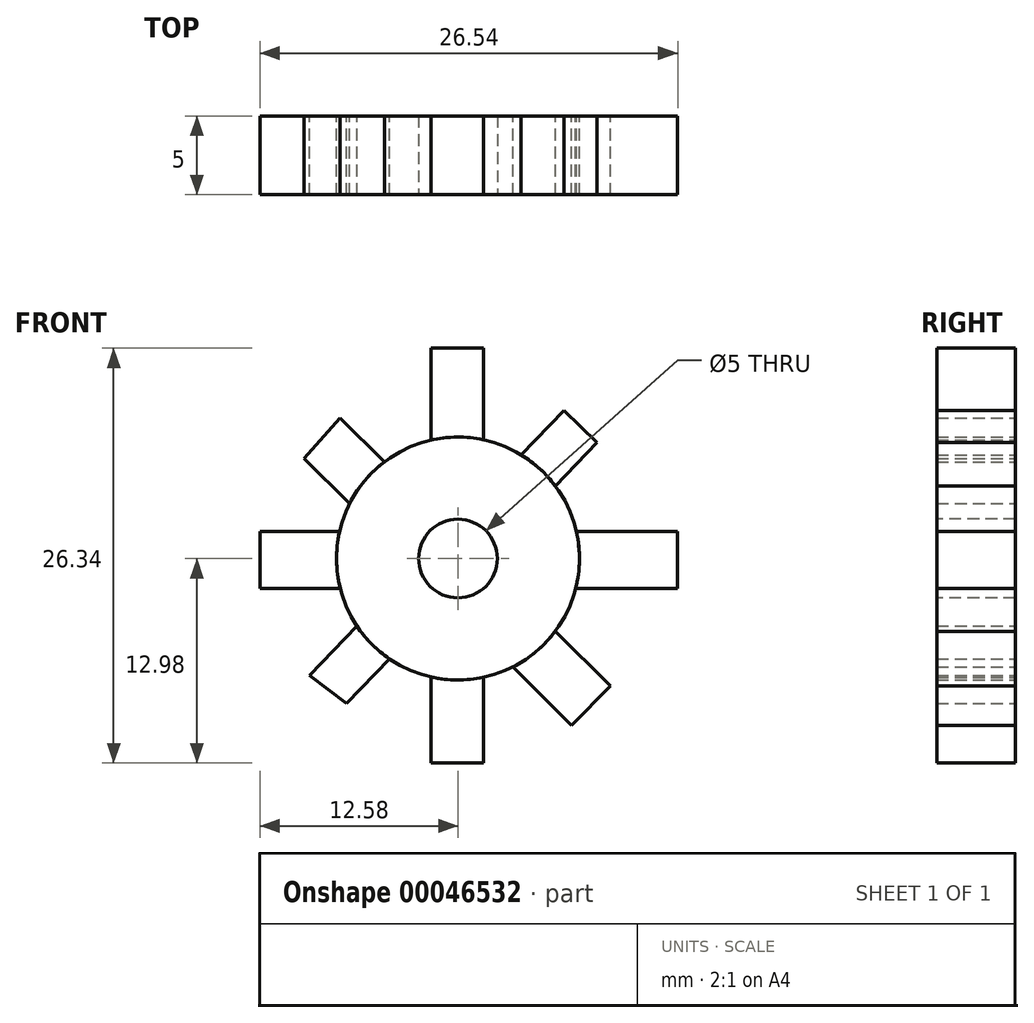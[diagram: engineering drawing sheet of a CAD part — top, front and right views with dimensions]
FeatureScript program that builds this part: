
annotation { "Feature Type Name" : "Feature", "Feature Type Description" : "" }
export const myFeature = defineFeature(function(context is Context, id is Id, definition is map)
    precondition{}
    {
        {
            var Q0;
            Q0=qCreatedBy(makeId("Front.planeOp"),FACE);
            var sketch = newSketch(context, id + "F0", { "sketchPlane" : qUnion([Q0])});
            skCircle(sketch, "E0", {"center": v(0, 0) * mm, "radius": 7.71 * mm});
            skSolve(sketch);
        }
        {
            var Q0;
            Q0=makeQuery(id+"F0.imprint","IMPRINT",FACE,{"disambiguationData":[TD([[makeQuery(id+"F0.imprint","IMPRINT",EDGE,{"derivedFrom":sQuery(id+"F0.wireOp",EDGE,"E0")}),1.0]])]});
            var sketch = newSketch(context, id + "F1", { "sketchPlane" : qUnion([Q0])});
            skLineSegment(sketch, "E1.bottom", {"start": v(-1.71, 13.36) * mm, "end": v(1.62, 13.36) * mm});
            skLineSegment(sketch, "E1.top", {"start": v(-1.71, -12.98) * mm, "end": v(1.62, -12.98) * mm});
            skLineSegment(sketch, "E1.left", {"start": v(-1.71, 13.36) * mm, "end": v(-1.71, -12.98) * mm});
            skLineSegment(sketch, "E1.right", {"start": v(1.62, 13.36) * mm, "end": v(1.62, -12.98) * mm});
            skSolve(sketch);
        }
        {
            var Q0;
            Q0=makeQuery(id+"F0.imprint","IMPRINT",FACE,{"disambiguationData":[TD([[makeQuery(id+"F0.imprint","IMPRINT",EDGE,{"derivedFrom":sQuery(id+"F0.wireOp",EDGE,"E0")}),1.0]])]});
            var sketch = newSketch(context, id + "F2", { "sketchPlane" : qUnion([Q0])});
            skLineSegment(sketch, "E2.bottom", {"start": v(-12.58, 1.7) * mm, "end": v(13.96, 1.7) * mm});
            skLineSegment(sketch, "E2.top", {"start": v(-12.58, -1.91) * mm, "end": v(13.96, -1.91) * mm});
            skLineSegment(sketch, "E2.left", {"start": v(-12.58, 1.7) * mm, "end": v(-12.58, -1.91) * mm});
            skLineSegment(sketch, "E2.right", {"start": v(13.96, 1.7) * mm, "end": v(13.96, -1.91) * mm});
            skSolve(sketch);
        }
        {
            var Q0;
            Q0=makeQuery(id+"F0.imprint","IMPRINT",FACE,{"disambiguationData":[TD([[makeQuery(id+"F0.imprint","IMPRINT",EDGE,{"derivedFrom":sQuery(id+"F0.wireOp",EDGE,"E0")}),1.0]])]});
            var sketch = newSketch(context, id + "F3", { "sketchPlane" : qUnion([Q0])});
            skLineSegment(sketch, "E3", {"start": v(-9.76, 6.37) * mm, "end": v(7.2, -10.6) * mm});
            skLineSegment(sketch, "E4", {"start": v(7.2, -10.6) * mm, "end": v(9.9, -7.9) * mm});
            skLineSegment(sketch, "E5", {"start": v(9.7, -8.1) * mm, "end": v(-7.48, 8.93) * mm});
            skLineSegment(sketch, "E6", {"start": v(-7.48, 8.93) * mm, "end": v(-9.76, 6.37) * mm});
            skSolve(sketch);
        }
        {
            var Q0;
            Q0=makeQuery(id+"F0.imprint","IMPRINT",FACE,{"disambiguationData":[TD([[makeQuery(id+"F0.imprint","IMPRINT",EDGE,{"derivedFrom":sQuery(id+"F0.wireOp",EDGE,"E0")}),1.0]])]});
            var sketch = newSketch(context, id + "F4", { "sketchPlane" : qUnion([Q0])});
            skLineSegment(sketch, "E7", {"start": v(-9.41, -7.41) * mm, "end": v(6.72, 9.41) * mm});
            skLineSegment(sketch, "E8", {"start": v(6.72, 9.41) * mm, "end": v(8.84, 7.38) * mm});
            skLineSegment(sketch, "E9", {"start": v(8.84, 7.38) * mm, "end": v(-7.07, -9.21) * mm});
            skLineSegment(sketch, "E10", {"start": v(-7.07, -9.21) * mm, "end": v(-9.41, -7.41) * mm});
            skSolve(sketch);
        }
        {
            var Q0;
            Q0=makeQuery(id+"F0.imprint","IMPRINT",FACE,{"disambiguationData":[TD([[makeQuery(id+"F0.imprint","IMPRINT",EDGE,{"derivedFrom":sQuery(id+"F0.wireOp",EDGE,"E0")}),1.0]])]});
            var Q1;
            {var subQ0=sQuery(id+"F4.wireOp",EDGE,"E10");Q1=makeQuery(id+"F4.imprint","IMPRINT",FACE,{"disambiguationData":[TD([[makeQuery(id+"F4.imprint","IMPRINT",EDGE,{"derivedFrom":subQ0}),-1.0]])]});}
            var Q2;
            {var subQ5=sQuery(id+"F2.wireOp",EDGE,"E2.left");Q2=makeQuery(id+"F2.imprint","IMPRINT",FACE,{"disambiguationData":[TD([[makeQuery(id+"F2.imprint","IMPRINT",EDGE,{"derivedFrom":subQ5}),1.0]])]});}
            var Q3;
            {var subQ5=sQuery(id+"F3.wireOp",EDGE,"E6");Q3=makeQuery(id+"F3.imprint","IMPRINT",FACE,{"disambiguationData":[TD([[makeQuery(id+"F3.imprint","IMPRINT",EDGE,{"derivedFrom":subQ5}),1.0]])]});}
            var Q4;
            {var subQ5=sQuery(id+"F1.wireOp",EDGE,"E1.bottom");Q4=makeQuery(id+"F1.imprint","IMPRINT",FACE,{"disambiguationData":[TD([[makeQuery(id+"F1.imprint","IMPRINT",EDGE,{"derivedFrom":subQ5}),-1.0]])]});}
            var Q5;
            {var subQ5=sQuery(id+"F4.wireOp",EDGE,"E8");Q5=makeQuery(id+"F4.imprint","IMPRINT",FACE,{"disambiguationData":[TD([[makeQuery(id+"F4.imprint","IMPRINT",EDGE,{"derivedFrom":subQ5}),-1.0]])]});}
            var Q6;
            {var subQ5=sQuery(id+"F2.wireOp",EDGE,"E2.right");Q6=makeQuery(id+"F2.imprint","IMPRINT",FACE,{"disambiguationData":[TD([[makeQuery(id+"F2.imprint","IMPRINT",EDGE,{"derivedFrom":subQ5}),-1.0]])]});}
            var Q7;
            {var subQ3=sQuery(id+"F3.wireOp",EDGE,"E3");var subQ5=sQuery(id+"F3.wireOp",EDGE,"E4");var subQ7=makeQuery(id+"F3.imprint","INTERSECT",VERTEX,{"derivedFrom":[subQ3,subQ5]});Q7=makeQuery(id+"F3.imprint","IMPRINT",FACE,{"disambiguationData":[TD([[makeQuery(id+"F3.imprint","IMPRINT",EDGE,{"disambiguationData":[TD([[subQ7,1.0]])],"derivedFrom":subQ3}),1.0]])]});}
            var Q8;
            {var subQ3=sQuery(id+"F1.wireOp",EDGE,"E1.top");Q8=makeQuery(id+"F1.imprint","IMPRINT",FACE,{"disambiguationData":[TD([[makeQuery(id+"F1.imprint","IMPRINT",EDGE,{"derivedFrom":subQ3}),1.0]])]});}
            extrude(context, id + "F5", {"entities" : qUnion([Q0, Q1, Q2, Q3, Q4, Q5, Q6, Q7, Q8]), "depth" : 5 * mm});
        }
        {
            var Q0;
            Q0=makeQuery(id+"F5.opExtrude","CAP_FACE",FACE,{"disambiguationData":[OSD([sQuery(id+"F0.wireOp",EDGE,"E0")])],"isStart":false});
            var sketch = newSketch(context, id + "F6", { "sketchPlane" : qUnion([Q0])});
            skCircle(sketch, "E11", {"center": v(0, 0) * mm, "radius": 2.37 * mm});
            skSolve(sketch);
        }
        {
            var Q0;
            Q0=sQuery(id+"F6.wireOp",VERTEX,"E11.center");
            var Q1;
            Q1=makeQuery(id+"F5.opExtrude","SWEPT_BODY",BODY,{"disambiguationData":[OSD([sQuery(id+"F0.wireOp",EDGE,"E0")])]});
            hole(context, id + "F7", {"style" : HoleStyle.SIMPLE, "holeDiameter" : 5 * mm, "endStyle" : HoleEndStyle.THROUGH, "locations" : qUnion([Q0]), "scope" : qUnion([Q1])});
        }
    });
